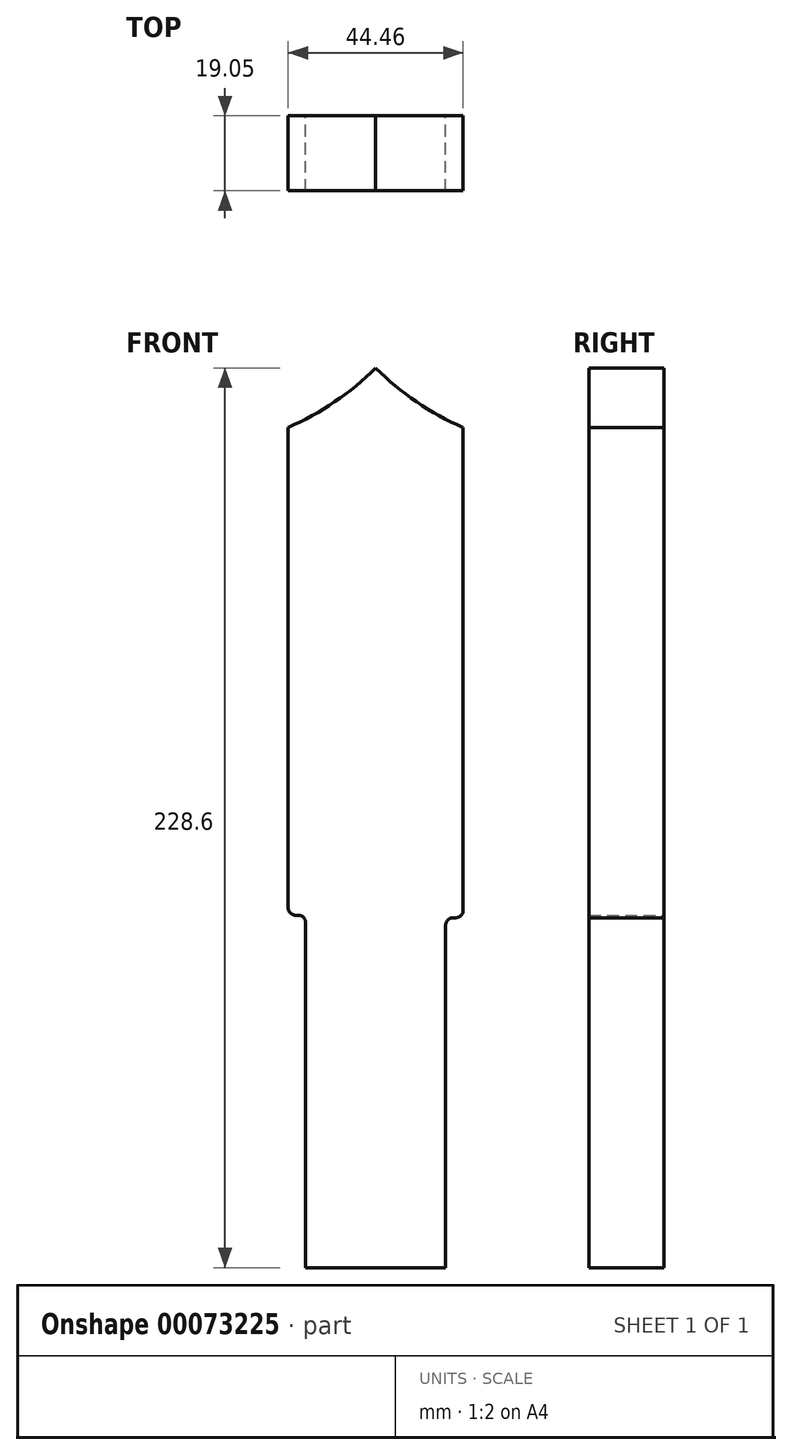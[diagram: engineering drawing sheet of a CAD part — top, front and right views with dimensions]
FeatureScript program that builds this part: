
annotation { "Feature Type Name" : "Feature", "Feature Type Description" : "" }
export const myFeature = defineFeature(function(context is Context, id is Id, definition is map)
    precondition{}
    {
        {
            var Q0;
            Q0=qCreatedBy(makeId("Front.planeOp"),FACE);
            var sketch = newSketch(context, id + "F0", { "sketchPlane" : qUnion([Q0])});
            skLineSegment(sketch, "E0.top", {"start": v(17.78, -114.3) * mm, "end": v(-17.78, -114.3) * mm});
            skLineSegment(sketch, "E0.left", {"start": v(22.23, 99.19) * mm, "end": v(22.22, -23.5) * mm});
            skLineSegment(sketch, "E0.right", {"start": v(-22.22, 99.19) * mm, "end": v(-22.23, -22.86) * mm});
            skPoint(sketch, "E0.middle", {"position": v(0, 0) * mm});
            skPoint(sketch, "E1.endSnap0", {"position": v(0, 114.3) * mm});
            skArc(sketch, "E2", {"start": v(-22.22, 99.19) * mm, "mid": v(-10.4, 105.7) * mm, "end": v(0, 114.3) * mm});
            skPoint(sketch, "E3.orphan", {"position": v(-22.22, 114.3) * mm});
            skPoint(sketch, "E1.start.orphan", {"position": v(0, 114.3) * mm});
            skPoint(sketch, "E4.start.orphan", {"position": v(0, 165.1) * mm});
            skArc(sketch, "E5.MirrorCS", {"start": v(22.22, 99.19) * mm, "mid": v(10.4, 105.7) * mm, "end": v(0, 114.3) * mm});
            skPoint(sketch, "E6", {"position": v(0, -25.4) * mm});
            skPoint(sketch, "E7", {"position": v(-17.78, -24.77) * mm});
            skPoint(sketch, "E8", {"position": v(17.78, -25.4) * mm});
            skLineSegment(sketch, "E9", {"start": v(-17.78, -26.67) * mm, "end": v(-17.78, -114.3) * mm});
            skLineSegment(sketch, "E10", {"start": v(17.78, -27.3) * mm, "end": v(17.78, -114.3) * mm});
            skLineSegment(sketch, "E11", {"start": v(-19.68, -24.77) * mm, "end": v(-20.32, -24.77) * mm});
            skLineSegment(sketch, "E12", {"start": v(19.69, -25.4) * mm, "end": v(20.32, -25.4) * mm});
            skPoint(sketch, "E13.orphan", {"position": v(22.22, -114.3) * mm});
            skPoint(sketch, "E14.orphan", {"position": v(-22.23, -114.3) * mm});
            skArc(sketch, "E15.filletArc", {"start": v(-17.78, -26.67) * mm, "mid": v(-18.34, -25.32) * mm, "end": v(-19.68, -24.77) * mm});
            skPoint(sketch, "E16.visualSharp", {"position": v(-22.22, -24.77) * mm});
            skArc(sketch, "E16.filletArc", {"start": v(-22.22, -22.86) * mm, "mid": v(-21.67, -24.2) * mm, "end": v(-20.32, -24.77) * mm});
            skArc(sketch, "E17.filletArc", {"start": v(19.69, -25.4) * mm, "mid": v(18.34, -25.96) * mm, "end": v(17.78, -27.3) * mm});
            skPoint(sketch, "E18.visualSharp", {"position": v(22.22, -25.4) * mm});
            skArc(sketch, "E18.filletArc", {"start": v(20.32, -25.4) * mm, "mid": v(21.67, -24.84) * mm, "end": v(22.23, -23.5) * mm});
            skPoint(sketch, "E19.orphan", {"position": v(22.23, 114.3) * mm});
            skSolve(sketch);
        }
        {
            var Q0;
            Q0=makeQuery(id+"F0.imprint","IMPRINT",FACE,{"disambiguationData":[TD([[makeQuery(id+"F0.imprint","IMPRINT",EDGE,{"derivedFrom":sQuery(id+"F0.wireOp",EDGE,"E0.top")}),-1.0]])]});
            extrude(context, id + "F1", {"entities" : qUnion([Q0]), "depth" : 19.05 * mm});
        }
    });
